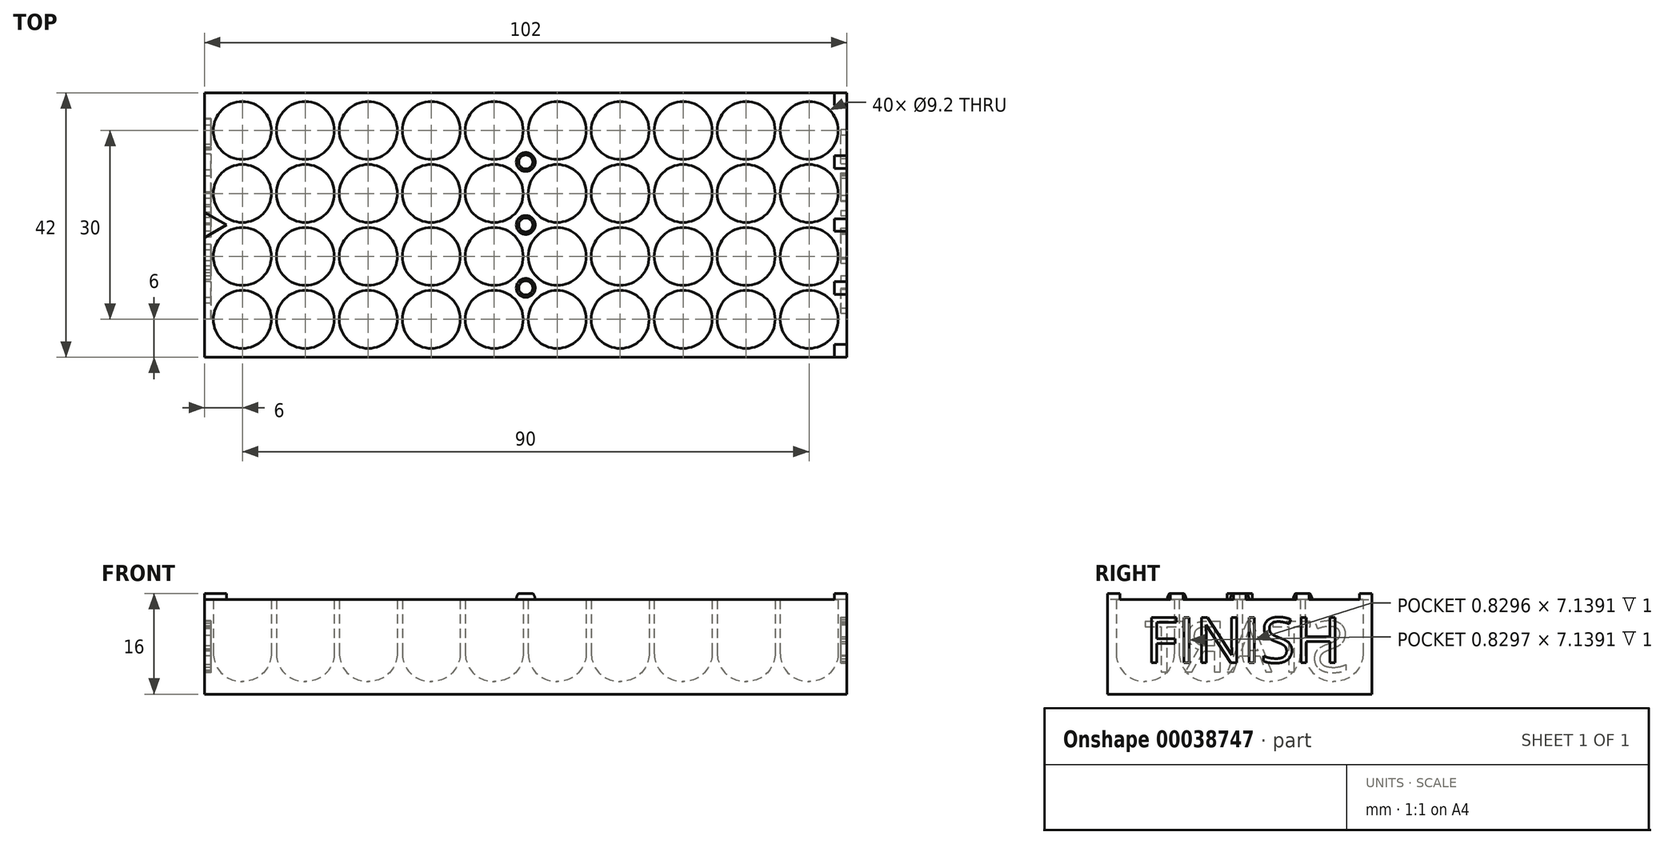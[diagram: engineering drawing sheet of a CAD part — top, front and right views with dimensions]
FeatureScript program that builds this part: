
annotation { "Feature Type Name" : "Feature", "Feature Type Description" : "" }
export const myFeature = defineFeature(function(context is Context, id is Id, definition is map)
    precondition{}
    {
        {
            var Q0;
            Q0=qCreatedBy(makeId("Top.planeOp"),FACE);
            var sketch = newSketch(context, id + "F0", { "sketchPlane" : qUnion([Q0])});
            skPoint(sketch, "E0", {"position": v(0, 0) * mm});
            skLineSegment(sketch, "E1", {"start": v(0, 0) * mm, "end": v(-10, 0) * mm, "construction": true});
            skCircle(sketch, "E2", {"center": v(0, 0) * mm, "radius": 4.6 * mm});
            skLineSegment(sketch, "E3", {"start": v(-10, 0) * mm, "end": v(-20, 0) * mm, "construction": true});
            skCircle(sketch, "E4", {"center": v(-10, 0) * mm, "radius": 4.6 * mm});
            skCircle(sketch, "E5", {"center": v(-20, 0) * mm, "radius": 4.6 * mm});
            skLineSegment(sketch, "E6", {"start": v(-20, 0) * mm, "end": v(-30, 0) * mm, "construction": true});
            skCircle(sketch, "E7", {"center": v(-30, 0) * mm, "radius": 4.6 * mm});
            skCircle(sketch, "E8.0.1.0", {"center": v(-30, 10) * mm, "radius": 4.6 * mm});
            skCircle(sketch, "E8.0.1.1", {"center": v(-20, 10) * mm, "radius": 4.6 * mm});
            skCircle(sketch, "E8.0.1.2", {"center": v(-10, 10) * mm, "radius": 4.6 * mm});
            skCircle(sketch, "E8.0.1.3", {"center": v(0, 10) * mm, "radius": 4.6 * mm});
            skCircle(sketch, "E8.0.2.0", {"center": v(-30, 20) * mm, "radius": 4.6 * mm});
            skCircle(sketch, "E8.0.2.1", {"center": v(-20, 20) * mm, "radius": 4.6 * mm});
            skCircle(sketch, "E8.0.2.2", {"center": v(-10, 20) * mm, "radius": 4.6 * mm});
            skCircle(sketch, "E8.0.2.3", {"center": v(0, 20) * mm, "radius": 4.6 * mm});
            skCircle(sketch, "E8.0.3.0", {"center": v(-30, 30) * mm, "radius": 4.6 * mm});
            skCircle(sketch, "E8.0.3.1", {"center": v(-20, 30) * mm, "radius": 4.6 * mm});
            skCircle(sketch, "E8.0.3.2", {"center": v(-10, 30) * mm, "radius": 4.6 * mm});
            skCircle(sketch, "E8.0.3.3", {"center": v(0, 30) * mm, "radius": 4.6 * mm});
            skCircle(sketch, "E8.0.4.0", {"center": v(-30, 40) * mm, "radius": 4.6 * mm});
            skCircle(sketch, "E8.0.4.1", {"center": v(-20, 40) * mm, "radius": 4.6 * mm});
            skCircle(sketch, "E8.0.4.2", {"center": v(-10, 40) * mm, "radius": 4.6 * mm});
            skCircle(sketch, "E8.0.4.3", {"center": v(0, 40) * mm, "radius": 4.6 * mm});
            skCircle(sketch, "E8.0.5.0", {"center": v(-30, 50) * mm, "radius": 4.6 * mm});
            skCircle(sketch, "E8.0.5.1", {"center": v(-20, 50) * mm, "radius": 4.6 * mm});
            skCircle(sketch, "E8.0.5.2", {"center": v(-10, 50) * mm, "radius": 4.6 * mm});
            skCircle(sketch, "E8.0.5.3", {"center": v(0, 50) * mm, "radius": 4.6 * mm});
            skCircle(sketch, "E8.0.6.0", {"center": v(-30, 60) * mm, "radius": 4.6 * mm});
            skCircle(sketch, "E8.0.6.1", {"center": v(-20, 60) * mm, "radius": 4.6 * mm});
            skCircle(sketch, "E8.0.6.2", {"center": v(-10, 60) * mm, "radius": 4.6 * mm});
            skCircle(sketch, "E8.0.6.3", {"center": v(0, 60) * mm, "radius": 4.6 * mm});
            skCircle(sketch, "E8.0.7.0", {"center": v(-30, 70) * mm, "radius": 4.6 * mm});
            skCircle(sketch, "E8.0.7.1", {"center": v(-20, 70) * mm, "radius": 4.6 * mm});
            skCircle(sketch, "E8.0.7.2", {"center": v(-10, 70) * mm, "radius": 4.6 * mm});
            skCircle(sketch, "E8.0.7.3", {"center": v(0, 70) * mm, "radius": 4.6 * mm});
            skCircle(sketch, "E8.0.8.0", {"center": v(-30, 80) * mm, "radius": 4.6 * mm});
            skCircle(sketch, "E8.0.8.1", {"center": v(-20, 80) * mm, "radius": 4.6 * mm});
            skCircle(sketch, "E8.0.8.2", {"center": v(-10, 80) * mm, "radius": 4.6 * mm});
            skCircle(sketch, "E8.0.8.3", {"center": v(0, 80) * mm, "radius": 4.6 * mm});
            skCircle(sketch, "E8.0.9.0", {"center": v(-30, 90) * mm, "radius": 4.6 * mm});
            skCircle(sketch, "E8.0.9.1", {"center": v(-20, 90) * mm, "radius": 4.6 * mm});
            skCircle(sketch, "E8.0.9.2", {"center": v(-10, 90) * mm, "radius": 4.6 * mm});
            skCircle(sketch, "E8.0.9.3", {"center": v(0, 90) * mm, "radius": 4.6 * mm});
            skLineSegment(sketch, "E8.direction2", {"start": v(-30, 0) * mm, "end": v(-30, 10) * mm, "construction": true});
            skLineSegment(sketch, "E9", {"start": v(0, 0) * mm, "end": v(6, 0) * mm, "construction": true});
            skLineSegment(sketch, "E10", {"start": v(0, 0) * mm, "end": v(0, -6) * mm, "construction": true});
            skLineSegment(sketch, "E11.bottom", {"start": v(6, -6) * mm, "end": v(-36, -6) * mm});
            skLineSegment(sketch, "E11.top", {"start": v(6, 96) * mm, "end": v(-36, 96) * mm});
            skLineSegment(sketch, "E11.left", {"start": v(6, -6) * mm, "end": v(6, 96) * mm});
            skLineSegment(sketch, "E11.right", {"start": v(-36, -6) * mm, "end": v(-36, 96) * mm});
            skSolve(sketch);
        }
        {
            var Q0;
            Q0 = qSketchRegion(id + "F0", true);
            extrude(context, id + "F1", {"entities" : qUnion([Q0]), "depth" : 15 * mm});
        }
        {
            var Q0;
            Q0=makeQuery(id+"F1.opExtrude","SWEPT_FACE",FACE,{"disambiguationData":[OSD([sQuery(id+"F0.wireOp",EDGE,"E11.bottom")])]});
            var sketch = newSketch(context, id + "F2", { "sketchPlane" : qUnion([Q0])});
            skLineSegment(sketch, "E12.bottom", {"start": v(-36, 0) * mm, "end": v(6, 0) * mm});
            skLineSegment(sketch, "E12.top", {"start": v(-36, 2) * mm, "end": v(6, 2) * mm});
            skLineSegment(sketch, "E12.left", {"start": v(-36, 0) * mm, "end": v(-36, 2) * mm});
            skLineSegment(sketch, "E12.right", {"start": v(6, 0) * mm, "end": v(6, 2) * mm});
            skSolve(sketch);
        }
        {
            var Q0;
            Q0 = qSketchRegion(id + "F2", true);
            extrude(context, id + "F3", {"entities" : qUnion([Q0]), "operationType" : NewBodyOperationType.ADD, "oppositeDirection" : true, "depth" : 102 * mm});
        }
        {
            var Q0;
            Q0=makeQuery(id+"F1.opExtrude","CAP_FACE",FACE,{"disambiguationData":[OSD([sQuery(id+"F0.wireOp",EDGE,"E2"),sQuery(id+"F0.wireOp",EDGE,"E4"),sQuery(id+"F0.wireOp",EDGE,"E5"),sQuery(id+"F0.wireOp",EDGE,"E7"),sQuery(id+"F0.wireOp",EDGE,"E8.0.1.0"),sQuery(id+"F0.wireOp",EDGE,"E8.0.1.1"),sQuery(id+"F0.wireOp",EDGE,"E8.0.1.2"),sQuery(id+"F0.wireOp",EDGE,"E8.0.1.3"),sQuery(id+"F0.wireOp",EDGE,"E8.0.2.0"),sQuery(id+"F0.wireOp",EDGE,"E8.0.2.1"),sQuery(id+"F0.wireOp",EDGE,"E8.0.2.2"),sQuery(id+"F0.wireOp",EDGE,"E8.0.2.3"),sQuery(id+"F0.wireOp",EDGE,"E8.0.3.0"),sQuery(id+"F0.wireOp",EDGE,"E8.0.3.1"),sQuery(id+"F0.wireOp",EDGE,"E8.0.3.2"),sQuery(id+"F0.wireOp",EDGE,"E8.0.3.3"),sQuery(id+"F0.wireOp",EDGE,"E8.0.4.0"),sQuery(id+"F0.wireOp",EDGE,"E8.0.4.1"),sQuery(id+"F0.wireOp",EDGE,"E8.0.4.2"),sQuery(id+"F0.wireOp",EDGE,"E8.0.4.3"),sQuery(id+"F0.wireOp",EDGE,"E8.0.5.0"),sQuery(id+"F0.wireOp",EDGE,"E8.0.5.1"),sQuery(id+"F0.wireOp",EDGE,"E8.0.5.2"),sQuery(id+"F0.wireOp",EDGE,"E8.0.5.3"),sQuery(id+"F0.wireOp",EDGE,"E8.0.6.0"),sQuery(id+"F0.wireOp",EDGE,"E8.0.6.1"),sQuery(id+"F0.wireOp",EDGE,"E8.0.6.2"),sQuery(id+"F0.wireOp",EDGE,"E8.0.6.3"),sQuery(id+"F0.wireOp",EDGE,"E8.0.7.0"),sQuery(id+"F0.wireOp",EDGE,"E8.0.7.1"),sQuery(id+"F0.wireOp",EDGE,"E8.0.7.2"),sQuery(id+"F0.wireOp",EDGE,"E8.0.7.3"),sQuery(id+"F0.wireOp",EDGE,"E8.0.8.0"),sQuery(id+"F0.wireOp",EDGE,"E8.0.8.1"),sQuery(id+"F0.wireOp",EDGE,"E8.0.8.2"),sQuery(id+"F0.wireOp",EDGE,"E8.0.8.3"),sQuery(id+"F0.wireOp",EDGE,"E8.0.9.0"),sQuery(id+"F0.wireOp",EDGE,"E8.0.9.1"),sQuery(id+"F0.wireOp",EDGE,"E8.0.9.2"),sQuery(id+"F0.wireOp",EDGE,"E8.0.9.3"),sQuery(id+"F0.wireOp",EDGE,"E11.bottom"),sQuery(id+"F0.wireOp",EDGE,"E11.top"),sQuery(id+"F0.wireOp",EDGE,"E11.left"),sQuery(id+"F0.wireOp",EDGE,"E11.right")])],"isStart":false});
            var sketch = newSketch(context, id + "F4", { "sketchPlane" : qUnion([Q0])});
            skLineSegment(sketch, "E13", {"start": v(-36, 96) * mm, "end": v(6, -6) * mm, "construction": true});
            skLineSegment(sketch, "E14", {"start": v(6, -6) * mm, "end": v(-36, -6) * mm, "construction": true});
            skLineSegment(sketch, "E15", {"start": v(-36, -6) * mm, "end": v(6, 96) * mm, "construction": true});
            skLineSegment(sketch, "E16", {"start": v(-16.5, 45) * mm, "end": v(-13.5, 45) * mm});
            skPoint(sketch, "E16.startSnap0", {"position": v(-15, 45) * mm});
            skLineSegment(sketch, "E17", {"start": v(-15, 45) * mm, "end": v(-5, 45) * mm, "construction": true});
            skLineSegment(sketch, "E18", {"start": v(-15, 45) * mm, "end": v(-25, 45) * mm, "construction": true});
            skLineSegment(sketch, "E19", {"start": v(-26.5, 45) * mm, "end": v(-23.5, 45) * mm});
            skLineSegment(sketch, "E20", {"start": v(-3.5, 45) * mm, "end": v(-6.5, 45) * mm});
            skArc(sketch, "E21", {"start": v(-23.5, 45) * mm, "mid": v(-25, 46.5) * mm, "end": v(-26.5, 45) * mm});
            skArc(sketch, "E22", {"start": v(-13.5, 45) * mm, "mid": v(-15, 46.5) * mm, "end": v(-16.5, 45) * mm});
            skArc(sketch, "E23", {"start": v(-3.5, 45) * mm, "mid": v(-5, 46.5) * mm, "end": v(-6.5, 45) * mm});
            skSolve(sketch);
        }
        {
            var Q0;
            Q0 = qSketchRegion(id + "F4", true);
            var Q1;
            Q1=sQuery(id+"F4.wireOp",EDGE,"E16");
            revolve(context, id + "F5", {"operationType" : NewBodyOperationType.ADD, "entities" : qUnion([Q0]), "axis" : qUnion([Q1]), "revolveType" : RevolveType.ONE_DIRECTION, "angle" : 180 * degree});
        }
        {
            var Q0;
            Q0=makeQuery(id+"F1.opExtrude","SWEPT_FACE",FACE,{"disambiguationData":[OSD([sQuery(id+"F0.wireOp",EDGE,"E11.bottom")])]});
            var sketch = newSketch(context, id + "F6", { "sketchPlane" : qUnion([Q0])});
            skText(sketch, "E24", { "text": "START", "fontName": "OpenSans-Regular.ttf"});
            const initialGuessF6  = {"E24": [-0.03248, 0.00352, 1, 0, 0.00807]};
            skSetInitialGuess(sketch, initialGuessF6);
            skSolve(sketch);
        }
        {
            var Q0;
            Q0 = qSketchRegion(id + "F6", true);
            extrude(context, id + "F7", {"entities" : qUnion([Q0]), "operationType" : NewBodyOperationType.REMOVE, "oppositeDirection" : true, "depth" : 1 * mm});
        }
        {
            var Q0;
            Q0=makeQuery(id+"F1.opExtrude","SWEPT_FACE",FACE,{"disambiguationData":[OSD([sQuery(id+"F0.wireOp",EDGE,"E11.top")])]});
            var sketch = newSketch(context, id + "F8", { "sketchPlane" : qUnion([Q0])});
            skText(sketch, "E25", { "text": "FINISH", "fontName": "OpenSans-Regular.ttf"});
            const initialGuessF8  = {"E25": [0, 0.00501, 1, 0, 0.0072]};
            skSetInitialGuess(sketch, initialGuessF8);
            skSolve(sketch);
        }
        {
            var Q0;
            Q0 = qSketchRegion(id + "F8", true);
            extrude(context, id + "F9", {"entities" : qUnion([Q0]), "operationType" : NewBodyOperationType.REMOVE, "oppositeDirection" : true, "depth" : 1 * mm});
        }
        {
            var Q0;
            Q0=makeQuery(id+"F1.opExtrude","CAP_FACE",FACE,{"disambiguationData":[OSD([sQuery(id+"F0.wireOp",EDGE,"E2"),sQuery(id+"F0.wireOp",EDGE,"E4"),sQuery(id+"F0.wireOp",EDGE,"E5"),sQuery(id+"F0.wireOp",EDGE,"E7"),sQuery(id+"F0.wireOp",EDGE,"E8.0.1.0"),sQuery(id+"F0.wireOp",EDGE,"E8.0.1.1"),sQuery(id+"F0.wireOp",EDGE,"E8.0.1.2"),sQuery(id+"F0.wireOp",EDGE,"E8.0.1.3"),sQuery(id+"F0.wireOp",EDGE,"E8.0.2.0"),sQuery(id+"F0.wireOp",EDGE,"E8.0.2.1"),sQuery(id+"F0.wireOp",EDGE,"E8.0.2.2"),sQuery(id+"F0.wireOp",EDGE,"E8.0.2.3"),sQuery(id+"F0.wireOp",EDGE,"E8.0.3.0"),sQuery(id+"F0.wireOp",EDGE,"E8.0.3.1"),sQuery(id+"F0.wireOp",EDGE,"E8.0.3.2"),sQuery(id+"F0.wireOp",EDGE,"E8.0.3.3"),sQuery(id+"F0.wireOp",EDGE,"E8.0.4.0"),sQuery(id+"F0.wireOp",EDGE,"E8.0.4.1"),sQuery(id+"F0.wireOp",EDGE,"E8.0.4.2"),sQuery(id+"F0.wireOp",EDGE,"E8.0.4.3"),sQuery(id+"F0.wireOp",EDGE,"E8.0.5.0"),sQuery(id+"F0.wireOp",EDGE,"E8.0.5.1"),sQuery(id+"F0.wireOp",EDGE,"E8.0.5.2"),sQuery(id+"F0.wireOp",EDGE,"E8.0.5.3"),sQuery(id+"F0.wireOp",EDGE,"E8.0.6.0"),sQuery(id+"F0.wireOp",EDGE,"E8.0.6.1"),sQuery(id+"F0.wireOp",EDGE,"E8.0.6.2"),sQuery(id+"F0.wireOp",EDGE,"E8.0.6.3"),sQuery(id+"F0.wireOp",EDGE,"E8.0.7.0"),sQuery(id+"F0.wireOp",EDGE,"E8.0.7.1"),sQuery(id+"F0.wireOp",EDGE,"E8.0.7.2"),sQuery(id+"F0.wireOp",EDGE,"E8.0.7.3"),sQuery(id+"F0.wireOp",EDGE,"E8.0.8.0"),sQuery(id+"F0.wireOp",EDGE,"E8.0.8.1"),sQuery(id+"F0.wireOp",EDGE,"E8.0.8.2"),sQuery(id+"F0.wireOp",EDGE,"E8.0.8.3"),sQuery(id+"F0.wireOp",EDGE,"E8.0.9.0"),sQuery(id+"F0.wireOp",EDGE,"E8.0.9.1"),sQuery(id+"F0.wireOp",EDGE,"E8.0.9.2"),sQuery(id+"F0.wireOp",EDGE,"E8.0.9.3"),sQuery(id+"F0.wireOp",EDGE,"E11.bottom"),sQuery(id+"F0.wireOp",EDGE,"E11.top"),sQuery(id+"F0.wireOp",EDGE,"E11.left"),sQuery(id+"F0.wireOp",EDGE,"E11.right")])],"isStart":false});
            var sketch = newSketch(context, id + "F10", { "sketchPlane" : qUnion([Q0])});
            skLineSegment(sketch, "E26", {"start": v(-17, -6) * mm, "end": v(-13, -6) * mm});
            skLineSegment(sketch, "E27", {"start": v(-13, -6) * mm, "end": v(-15, -2.54) * mm});
            skLineSegment(sketch, "E28", {"start": v(-15, -2.54) * mm, "end": v(-17, -6) * mm});
            skLineSegment(sketch, "E29", {"start": v(-15, 96) * mm, "end": v(-15, 95) * mm, "construction": true});
            skLineSegment(sketch, "E30.rect.bottom", {"start": v(-16, 96) * mm, "end": v(-14, 96) * mm});
            skLineSegment(sketch, "E30.rect.top", {"start": v(-16, 94) * mm, "end": v(-14, 94) * mm});
            skLineSegment(sketch, "E30.rect.left", {"start": v(-16, 96) * mm, "end": v(-16, 94) * mm});
            skLineSegment(sketch, "E30.rect.right", {"start": v(-14, 96) * mm, "end": v(-14, 94) * mm});
            skPoint(sketch, "E30.rect.middle", {"position": v(-15, 95) * mm});
            skLineSegment(sketch, "E31", {"start": v(-15, 95) * mm, "end": v(-25, 95) * mm, "construction": true});
            skPoint(sketch, "E31.endSnap0", {"position": v(-16, 95) * mm});
            skLineSegment(sketch, "E32", {"start": v(-25, 95) * mm, "end": v(-35, 95) * mm, "construction": true});
            skLineSegment(sketch, "E33", {"start": v(-15, 95) * mm, "end": v(-5, 95) * mm, "construction": true});
            skLineSegment(sketch, "E34", {"start": v(-5, 95) * mm, "end": v(5, 95) * mm, "construction": true});
            skLineSegment(sketch, "E35.rect.bottom", {"start": v(-26, 96) * mm, "end": v(-24, 96) * mm});
            skLineSegment(sketch, "E35.rect.top", {"start": v(-26, 94) * mm, "end": v(-24, 94) * mm});
            skLineSegment(sketch, "E35.rect.left", {"start": v(-26, 96) * mm, "end": v(-26, 94) * mm});
            skLineSegment(sketch, "E35.rect.right", {"start": v(-24, 96) * mm, "end": v(-24, 94) * mm});
            skPoint(sketch, "E35.rect.middle", {"position": v(-25, 95) * mm});
            skLineSegment(sketch, "E36.rect.bottom", {"start": v(-6, 96) * mm, "end": v(-4, 96) * mm});
            skLineSegment(sketch, "E36.rect.top", {"start": v(-6, 94) * mm, "end": v(-4, 94) * mm});
            skLineSegment(sketch, "E36.rect.left", {"start": v(-6, 96) * mm, "end": v(-6, 94) * mm});
            skLineSegment(sketch, "E36.rect.right", {"start": v(-4, 96) * mm, "end": v(-4, 94) * mm});
            skPoint(sketch, "E36.rect.middle", {"position": v(-5, 95) * mm});
            skLineSegment(sketch, "E37.rect.bottom", {"start": v(4, 96) * mm, "end": v(6, 96) * mm});
            skLineSegment(sketch, "E37.rect.top", {"start": v(4, 94) * mm, "end": v(6, 94) * mm});
            skLineSegment(sketch, "E37.rect.left", {"start": v(4, 96) * mm, "end": v(4, 94) * mm});
            skLineSegment(sketch, "E37.rect.right", {"start": v(6, 96) * mm, "end": v(6, 94) * mm});
            skPoint(sketch, "E37.rect.middle", {"position": v(5, 95) * mm});
            skLineSegment(sketch, "E38.rect.bottom", {"start": v(-34, 96) * mm, "end": v(-36, 96) * mm});
            skLineSegment(sketch, "E38.rect.top", {"start": v(-34, 94) * mm, "end": v(-36, 94) * mm});
            skLineSegment(sketch, "E38.rect.left", {"start": v(-34, 96) * mm, "end": v(-34, 94) * mm});
            skLineSegment(sketch, "E38.rect.right", {"start": v(-36, 96) * mm, "end": v(-36, 94) * mm});
            skPoint(sketch, "E38.rect.middle", {"position": v(-35, 95) * mm});
            skPoint(sketch, "E39", {"position": v(-15, -6) * mm});
            skSolve(sketch);
        }
        {
            var Q0;
            Q0 = qSketchRegion(id + "F10", true);
            extrude(context, id + "F11", {"entities" : qUnion([Q0]), "operationType" : NewBodyOperationType.ADD, "depth" : 1 * mm});
        }
        {
            var Q0;
            Q0=makeQuery(id+"F3.boolean.opBoolean","INTERSECT",EDGE,{"derivedFrom":[makeQuery(id+"F1.opExtrude","SWEPT_FACE",FACE,{"disambiguationData":[OSD([sQuery(id+"F0.wireOp",EDGE,"E7")])]}),makeQuery(id+"F3.opExtrude","SWEPT_FACE",FACE,{"disambiguationData":[OSD([sQuery(id+"F2.wireOp",EDGE,"E12.top")])]})]});
            var Q1;
            Q1=makeQuery(id+"F3.boolean.opBoolean","INTERSECT",EDGE,{"derivedFrom":[makeQuery(id+"F1.opExtrude","SWEPT_FACE",FACE,{"disambiguationData":[OSD([sQuery(id+"F0.wireOp",EDGE,"E8.0.1.0")])]}),makeQuery(id+"F3.opExtrude","SWEPT_FACE",FACE,{"disambiguationData":[OSD([sQuery(id+"F2.wireOp",EDGE,"E12.top")])]})]});
            var Q2;
            Q2=makeQuery(id+"F3.boolean.opBoolean","INTERSECT",EDGE,{"derivedFrom":[makeQuery(id+"F1.opExtrude","SWEPT_FACE",FACE,{"disambiguationData":[OSD([sQuery(id+"F0.wireOp",EDGE,"E8.0.2.0")])]}),makeQuery(id+"F3.opExtrude","SWEPT_FACE",FACE,{"disambiguationData":[OSD([sQuery(id+"F2.wireOp",EDGE,"E12.top")])]})]});
            var Q3;
            Q3=makeQuery(id+"F3.boolean.opBoolean","INTERSECT",EDGE,{"derivedFrom":[makeQuery(id+"F1.opExtrude","SWEPT_FACE",FACE,{"disambiguationData":[OSD([sQuery(id+"F0.wireOp",EDGE,"E8.0.3.0")])]}),makeQuery(id+"F3.opExtrude","SWEPT_FACE",FACE,{"disambiguationData":[OSD([sQuery(id+"F2.wireOp",EDGE,"E12.top")])]})]});
            var Q4;
            Q4=makeQuery(id+"F3.boolean.opBoolean","INTERSECT",EDGE,{"derivedFrom":[makeQuery(id+"F1.opExtrude","SWEPT_FACE",FACE,{"disambiguationData":[OSD([sQuery(id+"F0.wireOp",EDGE,"E8.0.4.0")])]}),makeQuery(id+"F3.opExtrude","SWEPT_FACE",FACE,{"disambiguationData":[OSD([sQuery(id+"F2.wireOp",EDGE,"E12.top")])]})]});
            var Q5;
            Q5=makeQuery(id+"F3.boolean.opBoolean","INTERSECT",EDGE,{"derivedFrom":[makeQuery(id+"F1.opExtrude","SWEPT_FACE",FACE,{"disambiguationData":[OSD([sQuery(id+"F0.wireOp",EDGE,"E8.0.5.0")])]}),makeQuery(id+"F3.opExtrude","SWEPT_FACE",FACE,{"disambiguationData":[OSD([sQuery(id+"F2.wireOp",EDGE,"E12.top")])]})]});
            var Q6;
            Q6=makeQuery(id+"F3.boolean.opBoolean","INTERSECT",EDGE,{"derivedFrom":[makeQuery(id+"F1.opExtrude","SWEPT_FACE",FACE,{"disambiguationData":[OSD([sQuery(id+"F0.wireOp",EDGE,"E8.0.6.0")])]}),makeQuery(id+"F3.opExtrude","SWEPT_FACE",FACE,{"disambiguationData":[OSD([sQuery(id+"F2.wireOp",EDGE,"E12.top")])]})]});
            var Q7;
            Q7=makeQuery(id+"F3.boolean.opBoolean","INTERSECT",EDGE,{"derivedFrom":[makeQuery(id+"F1.opExtrude","SWEPT_FACE",FACE,{"disambiguationData":[OSD([sQuery(id+"F0.wireOp",EDGE,"E8.0.7.0")])]}),makeQuery(id+"F3.opExtrude","SWEPT_FACE",FACE,{"disambiguationData":[OSD([sQuery(id+"F2.wireOp",EDGE,"E12.top")])]})]});
            var Q8;
            Q8=makeQuery(id+"F3.boolean.opBoolean","INTERSECT",EDGE,{"derivedFrom":[makeQuery(id+"F1.opExtrude","SWEPT_FACE",FACE,{"disambiguationData":[OSD([sQuery(id+"F0.wireOp",EDGE,"E8.0.8.0")])]}),makeQuery(id+"F3.opExtrude","SWEPT_FACE",FACE,{"disambiguationData":[OSD([sQuery(id+"F2.wireOp",EDGE,"E12.top")])]})]});
            var Q9;
            Q9=makeQuery(id+"F3.boolean.opBoolean","INTERSECT",EDGE,{"derivedFrom":[makeQuery(id+"F1.opExtrude","SWEPT_FACE",FACE,{"disambiguationData":[OSD([sQuery(id+"F0.wireOp",EDGE,"E8.0.9.0")])]}),makeQuery(id+"F3.opExtrude","SWEPT_FACE",FACE,{"disambiguationData":[OSD([sQuery(id+"F2.wireOp",EDGE,"E12.top")])]})]});
            var Q10;
            Q10=makeQuery(id+"F3.boolean.opBoolean","INTERSECT",EDGE,{"derivedFrom":[makeQuery(id+"F1.opExtrude","SWEPT_FACE",FACE,{"disambiguationData":[OSD([sQuery(id+"F0.wireOp",EDGE,"E5")])]}),makeQuery(id+"F3.opExtrude","SWEPT_FACE",FACE,{"disambiguationData":[OSD([sQuery(id+"F2.wireOp",EDGE,"E12.top")])]})]});
            var Q11;
            Q11=makeQuery(id+"F3.boolean.opBoolean","INTERSECT",EDGE,{"derivedFrom":[makeQuery(id+"F1.opExtrude","SWEPT_FACE",FACE,{"disambiguationData":[OSD([sQuery(id+"F0.wireOp",EDGE,"E8.0.1.1")])]}),makeQuery(id+"F3.opExtrude","SWEPT_FACE",FACE,{"disambiguationData":[OSD([sQuery(id+"F2.wireOp",EDGE,"E12.top")])]})]});
            var Q12;
            Q12=makeQuery(id+"F3.boolean.opBoolean","INTERSECT",EDGE,{"derivedFrom":[makeQuery(id+"F1.opExtrude","SWEPT_FACE",FACE,{"disambiguationData":[OSD([sQuery(id+"F0.wireOp",EDGE,"E8.0.2.1")])]}),makeQuery(id+"F3.opExtrude","SWEPT_FACE",FACE,{"disambiguationData":[OSD([sQuery(id+"F2.wireOp",EDGE,"E12.top")])]})]});
            var Q13;
            Q13=makeQuery(id+"F3.boolean.opBoolean","INTERSECT",EDGE,{"derivedFrom":[makeQuery(id+"F1.opExtrude","SWEPT_FACE",FACE,{"disambiguationData":[OSD([sQuery(id+"F0.wireOp",EDGE,"E8.0.3.1")])]}),makeQuery(id+"F3.opExtrude","SWEPT_FACE",FACE,{"disambiguationData":[OSD([sQuery(id+"F2.wireOp",EDGE,"E12.top")])]})]});
            var Q14;
            Q14=makeQuery(id+"F3.boolean.opBoolean","INTERSECT",EDGE,{"derivedFrom":[makeQuery(id+"F1.opExtrude","SWEPT_FACE",FACE,{"disambiguationData":[OSD([sQuery(id+"F0.wireOp",EDGE,"E8.0.4.1")])]}),makeQuery(id+"F3.opExtrude","SWEPT_FACE",FACE,{"disambiguationData":[OSD([sQuery(id+"F2.wireOp",EDGE,"E12.top")])]})]});
            var Q15;
            Q15=makeQuery(id+"F3.boolean.opBoolean","INTERSECT",EDGE,{"derivedFrom":[makeQuery(id+"F1.opExtrude","SWEPT_FACE",FACE,{"disambiguationData":[OSD([sQuery(id+"F0.wireOp",EDGE,"E8.0.5.1")])]}),makeQuery(id+"F3.opExtrude","SWEPT_FACE",FACE,{"disambiguationData":[OSD([sQuery(id+"F2.wireOp",EDGE,"E12.top")])]})]});
            var Q16;
            Q16=makeQuery(id+"F3.boolean.opBoolean","INTERSECT",EDGE,{"derivedFrom":[makeQuery(id+"F1.opExtrude","SWEPT_FACE",FACE,{"disambiguationData":[OSD([sQuery(id+"F0.wireOp",EDGE,"E8.0.6.1")])]}),makeQuery(id+"F3.opExtrude","SWEPT_FACE",FACE,{"disambiguationData":[OSD([sQuery(id+"F2.wireOp",EDGE,"E12.top")])]})]});
            var Q17;
            Q17=makeQuery(id+"F3.boolean.opBoolean","INTERSECT",EDGE,{"derivedFrom":[makeQuery(id+"F1.opExtrude","SWEPT_FACE",FACE,{"disambiguationData":[OSD([sQuery(id+"F0.wireOp",EDGE,"E8.0.7.1")])]}),makeQuery(id+"F3.opExtrude","SWEPT_FACE",FACE,{"disambiguationData":[OSD([sQuery(id+"F2.wireOp",EDGE,"E12.top")])]})]});
            var Q18;
            Q18=makeQuery(id+"F3.boolean.opBoolean","INTERSECT",EDGE,{"derivedFrom":[makeQuery(id+"F1.opExtrude","SWEPT_FACE",FACE,{"disambiguationData":[OSD([sQuery(id+"F0.wireOp",EDGE,"E8.0.8.1")])]}),makeQuery(id+"F3.opExtrude","SWEPT_FACE",FACE,{"disambiguationData":[OSD([sQuery(id+"F2.wireOp",EDGE,"E12.top")])]})]});
            var Q19;
            Q19=makeQuery(id+"F3.boolean.opBoolean","INTERSECT",EDGE,{"derivedFrom":[makeQuery(id+"F1.opExtrude","SWEPT_FACE",FACE,{"disambiguationData":[OSD([sQuery(id+"F0.wireOp",EDGE,"E8.0.9.1")])]}),makeQuery(id+"F3.opExtrude","SWEPT_FACE",FACE,{"disambiguationData":[OSD([sQuery(id+"F2.wireOp",EDGE,"E12.top")])]})]});
            var Q20;
            Q20=makeQuery(id+"F3.boolean.opBoolean","INTERSECT",EDGE,{"derivedFrom":[makeQuery(id+"F1.opExtrude","SWEPT_FACE",FACE,{"disambiguationData":[OSD([sQuery(id+"F0.wireOp",EDGE,"E4")])]}),makeQuery(id+"F3.opExtrude","SWEPT_FACE",FACE,{"disambiguationData":[OSD([sQuery(id+"F2.wireOp",EDGE,"E12.top")])]})]});
            var Q21;
            Q21=makeQuery(id+"F3.boolean.opBoolean","INTERSECT",EDGE,{"derivedFrom":[makeQuery(id+"F1.opExtrude","SWEPT_FACE",FACE,{"disambiguationData":[OSD([sQuery(id+"F0.wireOp",EDGE,"E8.0.1.2")])]}),makeQuery(id+"F3.opExtrude","SWEPT_FACE",FACE,{"disambiguationData":[OSD([sQuery(id+"F2.wireOp",EDGE,"E12.top")])]})]});
            var Q22;
            Q22=makeQuery(id+"F3.boolean.opBoolean","INTERSECT",EDGE,{"derivedFrom":[makeQuery(id+"F1.opExtrude","SWEPT_FACE",FACE,{"disambiguationData":[OSD([sQuery(id+"F0.wireOp",EDGE,"E8.0.2.2")])]}),makeQuery(id+"F3.opExtrude","SWEPT_FACE",FACE,{"disambiguationData":[OSD([sQuery(id+"F2.wireOp",EDGE,"E12.top")])]})]});
            var Q23;
            Q23=makeQuery(id+"F3.boolean.opBoolean","INTERSECT",EDGE,{"derivedFrom":[makeQuery(id+"F1.opExtrude","SWEPT_FACE",FACE,{"disambiguationData":[OSD([sQuery(id+"F0.wireOp",EDGE,"E8.0.3.2")])]}),makeQuery(id+"F3.opExtrude","SWEPT_FACE",FACE,{"disambiguationData":[OSD([sQuery(id+"F2.wireOp",EDGE,"E12.top")])]})]});
            var Q24;
            Q24=makeQuery(id+"F3.boolean.opBoolean","INTERSECT",EDGE,{"derivedFrom":[makeQuery(id+"F1.opExtrude","SWEPT_FACE",FACE,{"disambiguationData":[OSD([sQuery(id+"F0.wireOp",EDGE,"E8.0.4.2")])]}),makeQuery(id+"F3.opExtrude","SWEPT_FACE",FACE,{"disambiguationData":[OSD([sQuery(id+"F2.wireOp",EDGE,"E12.top")])]})]});
            var Q25;
            Q25=makeQuery(id+"F3.boolean.opBoolean","INTERSECT",EDGE,{"derivedFrom":[makeQuery(id+"F1.opExtrude","SWEPT_FACE",FACE,{"disambiguationData":[OSD([sQuery(id+"F0.wireOp",EDGE,"E8.0.5.2")])]}),makeQuery(id+"F3.opExtrude","SWEPT_FACE",FACE,{"disambiguationData":[OSD([sQuery(id+"F2.wireOp",EDGE,"E12.top")])]})]});
            var Q26;
            Q26=makeQuery(id+"F3.boolean.opBoolean","INTERSECT",EDGE,{"derivedFrom":[makeQuery(id+"F1.opExtrude","SWEPT_FACE",FACE,{"disambiguationData":[OSD([sQuery(id+"F0.wireOp",EDGE,"E8.0.6.2")])]}),makeQuery(id+"F3.opExtrude","SWEPT_FACE",FACE,{"disambiguationData":[OSD([sQuery(id+"F2.wireOp",EDGE,"E12.top")])]})]});
            var Q27;
            Q27=makeQuery(id+"F3.boolean.opBoolean","INTERSECT",EDGE,{"derivedFrom":[makeQuery(id+"F1.opExtrude","SWEPT_FACE",FACE,{"disambiguationData":[OSD([sQuery(id+"F0.wireOp",EDGE,"E8.0.7.2")])]}),makeQuery(id+"F3.opExtrude","SWEPT_FACE",FACE,{"disambiguationData":[OSD([sQuery(id+"F2.wireOp",EDGE,"E12.top")])]})]});
            var Q28;
            Q28=makeQuery(id+"F3.boolean.opBoolean","INTERSECT",EDGE,{"derivedFrom":[makeQuery(id+"F1.opExtrude","SWEPT_FACE",FACE,{"disambiguationData":[OSD([sQuery(id+"F0.wireOp",EDGE,"E8.0.8.2")])]}),makeQuery(id+"F3.opExtrude","SWEPT_FACE",FACE,{"disambiguationData":[OSD([sQuery(id+"F2.wireOp",EDGE,"E12.top")])]})]});
            var Q29;
            Q29=makeQuery(id+"F3.boolean.opBoolean","INTERSECT",EDGE,{"derivedFrom":[makeQuery(id+"F1.opExtrude","SWEPT_FACE",FACE,{"disambiguationData":[OSD([sQuery(id+"F0.wireOp",EDGE,"E8.0.9.2")])]}),makeQuery(id+"F3.opExtrude","SWEPT_FACE",FACE,{"disambiguationData":[OSD([sQuery(id+"F2.wireOp",EDGE,"E12.top")])]})]});
            var Q30;
            Q30=makeQuery(id+"F3.boolean.opBoolean","INTERSECT",EDGE,{"derivedFrom":[makeQuery(id+"F1.opExtrude","SWEPT_FACE",FACE,{"disambiguationData":[OSD([sQuery(id+"F0.wireOp",EDGE,"E2")])]}),makeQuery(id+"F3.opExtrude","SWEPT_FACE",FACE,{"disambiguationData":[OSD([sQuery(id+"F2.wireOp",EDGE,"E12.top")])]})]});
            var Q31;
            Q31=makeQuery(id+"F3.boolean.opBoolean","INTERSECT",EDGE,{"derivedFrom":[makeQuery(id+"F1.opExtrude","SWEPT_FACE",FACE,{"disambiguationData":[OSD([sQuery(id+"F0.wireOp",EDGE,"E8.0.1.3")])]}),makeQuery(id+"F3.opExtrude","SWEPT_FACE",FACE,{"disambiguationData":[OSD([sQuery(id+"F2.wireOp",EDGE,"E12.top")])]})]});
            var Q32;
            Q32=makeQuery(id+"F3.boolean.opBoolean","INTERSECT",EDGE,{"derivedFrom":[makeQuery(id+"F1.opExtrude","SWEPT_FACE",FACE,{"disambiguationData":[OSD([sQuery(id+"F0.wireOp",EDGE,"E8.0.2.3")])]}),makeQuery(id+"F3.opExtrude","SWEPT_FACE",FACE,{"disambiguationData":[OSD([sQuery(id+"F2.wireOp",EDGE,"E12.top")])]})]});
            var Q33;
            Q33=makeQuery(id+"F3.boolean.opBoolean","INTERSECT",EDGE,{"derivedFrom":[makeQuery(id+"F1.opExtrude","SWEPT_FACE",FACE,{"disambiguationData":[OSD([sQuery(id+"F0.wireOp",EDGE,"E8.0.3.3")])]}),makeQuery(id+"F3.opExtrude","SWEPT_FACE",FACE,{"disambiguationData":[OSD([sQuery(id+"F2.wireOp",EDGE,"E12.top")])]})]});
            var Q34;
            Q34=makeQuery(id+"F3.boolean.opBoolean","INTERSECT",EDGE,{"derivedFrom":[makeQuery(id+"F1.opExtrude","SWEPT_FACE",FACE,{"disambiguationData":[OSD([sQuery(id+"F0.wireOp",EDGE,"E8.0.4.3")])]}),makeQuery(id+"F3.opExtrude","SWEPT_FACE",FACE,{"disambiguationData":[OSD([sQuery(id+"F2.wireOp",EDGE,"E12.top")])]})]});
            var Q35;
            Q35=makeQuery(id+"F3.boolean.opBoolean","INTERSECT",EDGE,{"derivedFrom":[makeQuery(id+"F1.opExtrude","SWEPT_FACE",FACE,{"disambiguationData":[OSD([sQuery(id+"F0.wireOp",EDGE,"E8.0.5.3")])]}),makeQuery(id+"F3.opExtrude","SWEPT_FACE",FACE,{"disambiguationData":[OSD([sQuery(id+"F2.wireOp",EDGE,"E12.top")])]})]});
            var Q36;
            Q36=makeQuery(id+"F3.boolean.opBoolean","INTERSECT",EDGE,{"derivedFrom":[makeQuery(id+"F1.opExtrude","SWEPT_FACE",FACE,{"disambiguationData":[OSD([sQuery(id+"F0.wireOp",EDGE,"E8.0.6.3")])]}),makeQuery(id+"F3.opExtrude","SWEPT_FACE",FACE,{"disambiguationData":[OSD([sQuery(id+"F2.wireOp",EDGE,"E12.top")])]})]});
            var Q37;
            Q37=makeQuery(id+"F3.boolean.opBoolean","INTERSECT",EDGE,{"derivedFrom":[makeQuery(id+"F1.opExtrude","SWEPT_FACE",FACE,{"disambiguationData":[OSD([sQuery(id+"F0.wireOp",EDGE,"E8.0.7.3")])]}),makeQuery(id+"F3.opExtrude","SWEPT_FACE",FACE,{"disambiguationData":[OSD([sQuery(id+"F2.wireOp",EDGE,"E12.top")])]})]});
            var Q38;
            Q38=makeQuery(id+"F3.boolean.opBoolean","INTERSECT",EDGE,{"derivedFrom":[makeQuery(id+"F1.opExtrude","SWEPT_FACE",FACE,{"disambiguationData":[OSD([sQuery(id+"F0.wireOp",EDGE,"E8.0.8.3")])]}),makeQuery(id+"F3.opExtrude","SWEPT_FACE",FACE,{"disambiguationData":[OSD([sQuery(id+"F2.wireOp",EDGE,"E12.top")])]})]});
            var Q39;
            Q39=makeQuery(id+"F3.boolean.opBoolean","INTERSECT",EDGE,{"derivedFrom":[makeQuery(id+"F1.opExtrude","SWEPT_FACE",FACE,{"disambiguationData":[OSD([sQuery(id+"F0.wireOp",EDGE,"E8.0.9.3")])]}),makeQuery(id+"F3.opExtrude","SWEPT_FACE",FACE,{"disambiguationData":[OSD([sQuery(id+"F2.wireOp",EDGE,"E12.top")])]})]});
            fillet(context, id + "F12", {"entities" : qUnion([Q0, Q1, Q2, Q3, Q4, Q5, Q6, Q7, Q8, Q9, Q10, Q11, Q12, Q13, Q14, Q15, Q16, Q17, Q18, Q19, Q20, Q21, Q22, Q23, Q24, Q25, Q26, Q27, Q28, Q29, Q30, Q31, Q32, Q33, Q34, Q35, Q36, Q37, Q38, Q39]), "radius" : 4.5 * mm, "tangentPropagation" : true, "allowEdgeOverflow" : false});
        }
        {
            var Q0;
            Q0=makeQuery(id+"F11.opExtrude","CAP_FACE",FACE,{"disambiguationData":[OSD([sQuery(id+"F10.wireOp",EDGE,"E26"),sQuery(id+"F10.wireOp",EDGE,"E27"),sQuery(id+"F10.wireOp",EDGE,"E28")])],"isStart":false});
            var sketch = newSketch(context, id + "F13", { "sketchPlane" : qUnion([Q0])});
            skCircle(sketch, "E40.0.0", {"center": v(-15, 45) * mm, "radius": 1.5 * mm});
            skCircle(sketch, "E41.0.0", {"center": v(-25, 45) * mm, "radius": 1.5 * mm});
            skCircle(sketch, "E42.0.0", {"center": v(-5, 45) * mm, "radius": 1.5 * mm});
            skSolve(sketch);
        }
        {
            var Q0;
            Q0 = qSketchRegion(id + "F13", true);
            extrude(context, id + "F14", {"entities" : qUnion([Q0]), "operationType" : NewBodyOperationType.REMOVE, "endBound" : BoundingType.THROUGH_ALL, "depth" : 25 * mm});
        }
        {
            var Q0;
            Q0=makeQuery(id+"F1.opExtrude","SWEPT_BODY",BODY,{"disambiguationData":[OSD([sQuery(id+"F0.wireOp",EDGE,"E2"),sQuery(id+"F0.wireOp",EDGE,"E4"),sQuery(id+"F0.wireOp",EDGE,"E5"),sQuery(id+"F0.wireOp",EDGE,"E7"),sQuery(id+"F0.wireOp",EDGE,"E8.0.1.0"),sQuery(id+"F0.wireOp",EDGE,"E8.0.1.1"),sQuery(id+"F0.wireOp",EDGE,"E8.0.1.2"),sQuery(id+"F0.wireOp",EDGE,"E8.0.1.3"),sQuery(id+"F0.wireOp",EDGE,"E8.0.2.0"),sQuery(id+"F0.wireOp",EDGE,"E8.0.2.1"),sQuery(id+"F0.wireOp",EDGE,"E8.0.2.2"),sQuery(id+"F0.wireOp",EDGE,"E8.0.2.3"),sQuery(id+"F0.wireOp",EDGE,"E8.0.3.0"),sQuery(id+"F0.wireOp",EDGE,"E8.0.3.1"),sQuery(id+"F0.wireOp",EDGE,"E8.0.3.2"),sQuery(id+"F0.wireOp",EDGE,"E8.0.3.3"),sQuery(id+"F0.wireOp",EDGE,"E8.0.4.0"),sQuery(id+"F0.wireOp",EDGE,"E8.0.4.1"),sQuery(id+"F0.wireOp",EDGE,"E8.0.4.2"),sQuery(id+"F0.wireOp",EDGE,"E8.0.4.3"),sQuery(id+"F0.wireOp",EDGE,"E8.0.5.0"),sQuery(id+"F0.wireOp",EDGE,"E8.0.5.1"),sQuery(id+"F0.wireOp",EDGE,"E8.0.5.2"),sQuery(id+"F0.wireOp",EDGE,"E8.0.5.3"),sQuery(id+"F0.wireOp",EDGE,"E8.0.6.0"),sQuery(id+"F0.wireOp",EDGE,"E8.0.6.1"),sQuery(id+"F0.wireOp",EDGE,"E8.0.6.2"),sQuery(id+"F0.wireOp",EDGE,"E8.0.6.3"),sQuery(id+"F0.wireOp",EDGE,"E8.0.7.0"),sQuery(id+"F0.wireOp",EDGE,"E8.0.7.1"),sQuery(id+"F0.wireOp",EDGE,"E8.0.7.2"),sQuery(id+"F0.wireOp",EDGE,"E8.0.7.3"),sQuery(id+"F0.wireOp",EDGE,"E8.0.8.0"),sQuery(id+"F0.wireOp",EDGE,"E8.0.8.1"),sQuery(id+"F0.wireOp",EDGE,"E8.0.8.2"),sQuery(id+"F0.wireOp",EDGE,"E8.0.8.3"),sQuery(id+"F0.wireOp",EDGE,"E8.0.9.0"),sQuery(id+"F0.wireOp",EDGE,"E8.0.9.1"),sQuery(id+"F0.wireOp",EDGE,"E8.0.9.2"),sQuery(id+"F0.wireOp",EDGE,"E8.0.9.3"),sQuery(id+"F0.wireOp",EDGE,"E11.bottom"),sQuery(id+"F0.wireOp",EDGE,"E11.top"),sQuery(id+"F0.wireOp",EDGE,"E11.left"),sQuery(id+"F0.wireOp",EDGE,"E11.right")])]});
            var Q1;
            Q1=makeQuery(id+"F1.opExtrude","SWEPT_EDGE",EDGE,{"disambiguationData":[OSD([sQuery(id+"F0.wireOp",EDGE,"E11.bottom"),sQuery(id+"F0.wireOp",EDGE,"E11.right")])]});
            transform(context, id + "F15", {"entities" : qUnion([Q0]), "transformType" : TransformType.ROTATION, "transformAxis" : qUnion([Q1]), "angle" : 90 * degree, "makeCopy" : false});
        }
        {
            var Q0;
            Q0=makeQuery(id+"F1.opExtrude","SWEPT_BODY",BODY,{"disambiguationData":[OSD([sQuery(id+"F0.wireOp",EDGE,"E2"),sQuery(id+"F0.wireOp",EDGE,"E4"),sQuery(id+"F0.wireOp",EDGE,"E5"),sQuery(id+"F0.wireOp",EDGE,"E7"),sQuery(id+"F0.wireOp",EDGE,"E8.0.1.0"),sQuery(id+"F0.wireOp",EDGE,"E8.0.1.1"),sQuery(id+"F0.wireOp",EDGE,"E8.0.1.2"),sQuery(id+"F0.wireOp",EDGE,"E8.0.1.3"),sQuery(id+"F0.wireOp",EDGE,"E8.0.2.0"),sQuery(id+"F0.wireOp",EDGE,"E8.0.2.1"),sQuery(id+"F0.wireOp",EDGE,"E8.0.2.2"),sQuery(id+"F0.wireOp",EDGE,"E8.0.2.3"),sQuery(id+"F0.wireOp",EDGE,"E8.0.3.0"),sQuery(id+"F0.wireOp",EDGE,"E8.0.3.1"),sQuery(id+"F0.wireOp",EDGE,"E8.0.3.2"),sQuery(id+"F0.wireOp",EDGE,"E8.0.3.3"),sQuery(id+"F0.wireOp",EDGE,"E8.0.4.0"),sQuery(id+"F0.wireOp",EDGE,"E8.0.4.1"),sQuery(id+"F0.wireOp",EDGE,"E8.0.4.2"),sQuery(id+"F0.wireOp",EDGE,"E8.0.4.3"),sQuery(id+"F0.wireOp",EDGE,"E8.0.5.0"),sQuery(id+"F0.wireOp",EDGE,"E8.0.5.1"),sQuery(id+"F0.wireOp",EDGE,"E8.0.5.2"),sQuery(id+"F0.wireOp",EDGE,"E8.0.5.3"),sQuery(id+"F0.wireOp",EDGE,"E8.0.6.0"),sQuery(id+"F0.wireOp",EDGE,"E8.0.6.1"),sQuery(id+"F0.wireOp",EDGE,"E8.0.6.2"),sQuery(id+"F0.wireOp",EDGE,"E8.0.6.3"),sQuery(id+"F0.wireOp",EDGE,"E8.0.7.0"),sQuery(id+"F0.wireOp",EDGE,"E8.0.7.1"),sQuery(id+"F0.wireOp",EDGE,"E8.0.7.2"),sQuery(id+"F0.wireOp",EDGE,"E8.0.7.3"),sQuery(id+"F0.wireOp",EDGE,"E8.0.8.0"),sQuery(id+"F0.wireOp",EDGE,"E8.0.8.1"),sQuery(id+"F0.wireOp",EDGE,"E8.0.8.2"),sQuery(id+"F0.wireOp",EDGE,"E8.0.8.3"),sQuery(id+"F0.wireOp",EDGE,"E8.0.9.0"),sQuery(id+"F0.wireOp",EDGE,"E8.0.9.1"),sQuery(id+"F0.wireOp",EDGE,"E8.0.9.2"),sQuery(id+"F0.wireOp",EDGE,"E8.0.9.3"),sQuery(id+"F0.wireOp",EDGE,"E11.bottom"),sQuery(id+"F0.wireOp",EDGE,"E11.top"),sQuery(id+"F0.wireOp",EDGE,"E11.left"),sQuery(id+"F0.wireOp",EDGE,"E11.right")])]});
            transform(context, id + "F16", {"entities" : qUnion([Q0]), "transformType" : TransformType.TRANSLATION_3D, "dx" : 0 * mm, "dy" : 70 * mm, "dz" : 0 * mm, "makeCopy" : false});
        }
    });
